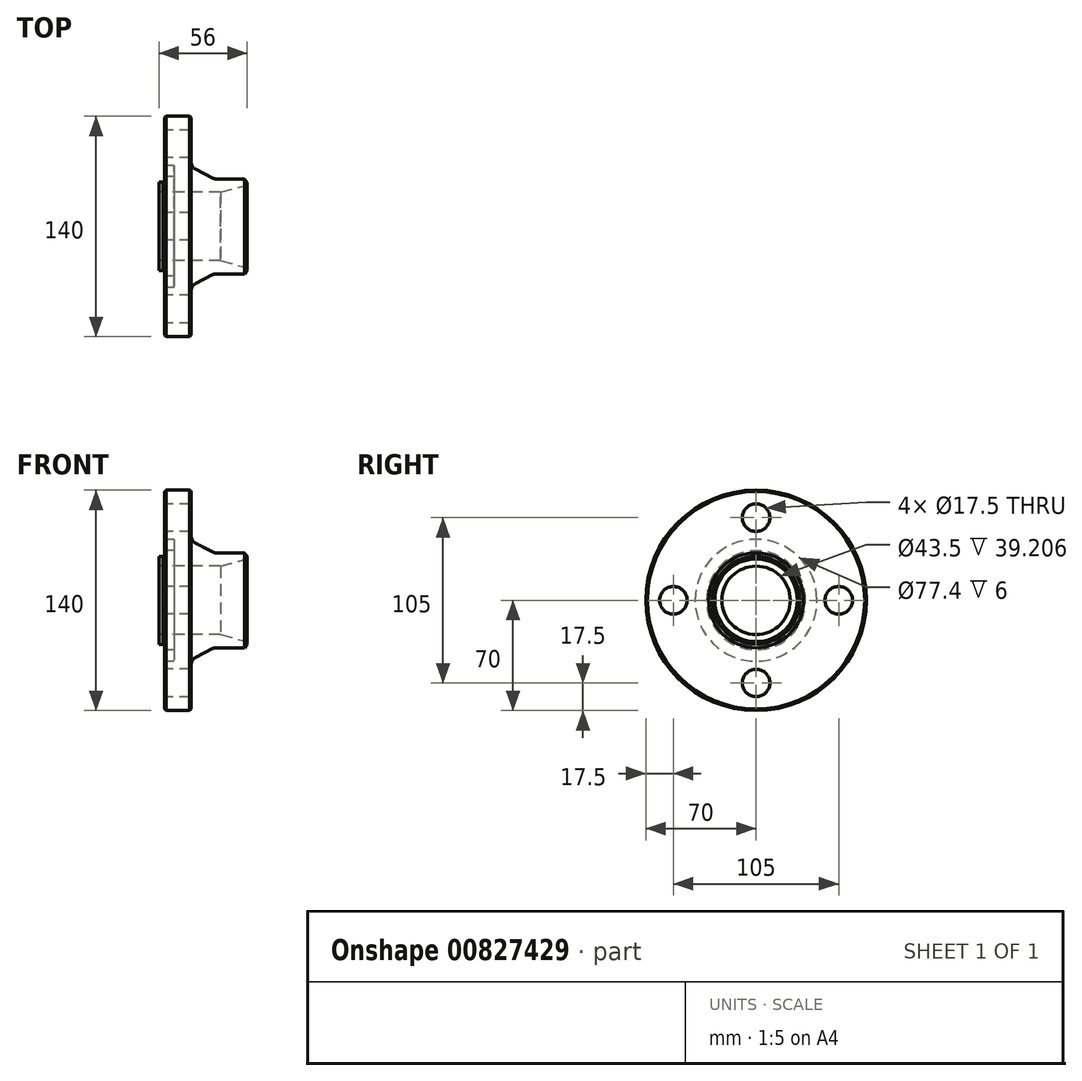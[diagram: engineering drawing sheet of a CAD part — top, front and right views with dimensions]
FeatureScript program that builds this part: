
annotation { "Feature Type Name" : "Feature", "Feature Type Description" : "" }
export const myFeature = defineFeature(function(context is Context, id is Id, definition is map)
    precondition{}
    {
        {
            var Q0;
            Q0=qCreatedBy(makeId("Front.planeOp"),FACE);
            var sketch = newSketch(context, id + "F0", { "sketchPlane" : qUnion([Q0])});
            skLineSegment(sketch, "E0", {"start": v(0, 0) * mm, "end": v(88.97, 0) * mm, "construction": true});
            skLineSegment(sketch, "E1", {"start": v(35.7, 21.75) * mm, "end": v(-3.5, 21.75) * mm});
            skLineSegment(sketch, "E2.trimOffspring", {"start": v(0, 28) * mm, "end": v(0, 31.5) * mm});
            skLineSegment(sketch, "E3", {"start": v(50.73, 30.15) * mm, "end": v(31.58, 30.15) * mm});
            skLineSegment(sketch, "E4", {"start": v(31.58, 30.15) * mm, "end": v(17, 37.7) * mm});
            skLineSegment(sketch, "E5", {"start": v(17, 37.7) * mm, "end": v(17, 70) * mm});
            skLineSegment(sketch, "E6", {"start": v(17, 70) * mm, "end": v(0, 70) * mm});
            skLineSegment(sketch, "E7", {"start": v(0, 31.5) * mm, "end": v(6, 31.5) * mm});
            skLineSegment(sketch, "E8", {"start": v(6, 31.5) * mm, "end": v(6, 38.7) * mm});
            skLineSegment(sketch, "E9", {"start": v(6, 38.7) * mm, "end": v(0, 38.7) * mm});
            skLineSegment(sketch, "E10.trimOffspring", {"start": v(0, 38.7) * mm, "end": v(0, 70) * mm});
            skLineSegment(sketch, "E11", {"start": v(-3.5, 28) * mm, "end": v(-3.5, 21.75) * mm});
            skPoint(sketch, "E12.orphan", {"position": v(0, 21.75) * mm});
            skLineSegment(sketch, "E13", {"start": v(0, 28) * mm, "end": v(-3.5, 28) * mm});
            skLineSegment(sketch, "E14", {"start": v(35.7, 21.75) * mm, "end": v(52.5, 26.25) * mm});
            skLineSegment(sketch, "E15", {"start": v(52.5, 26.25) * mm, "end": v(52.5, 27.84) * mm});
            skLineSegment(sketch, "E16", {"start": v(52.5, 27.84) * mm, "end": v(50.73, 30.15) * mm});
            skSolve(sketch);
        }
        {
            var Q0;
            Q0=makeQuery(id+"F0.imprint","IMPRINT",FACE,{"disambiguationData":[TD([[makeQuery(id+"F0.imprint","IMPRINT",EDGE,{"derivedFrom":sQuery(id+"F0.wireOp",EDGE,"E1")}),-1.0]])]});
            var Q1;
            Q1=sQuery(id+"F0.wireOp",EDGE,"E0");
            revolve(context, id + "F1", {"surfaceOperationType" : NewSurfaceOperationType.NEW, "entities" : qUnion([Q0]), "axis" : qUnion([Q1]), "revolveType" : RevolveType.FULL});
        }
        {
            var Q0;
            Q0=makeQuery(id+"F1.opRevolve","SWEPT_EDGE",EDGE,{"disambiguationData":[OSD([sQuery(id+"F0.wireOp",EDGE,"ZkZXfTss-pbWi-7Jdx-PPOn-aKjTsRns9WXB"),sQuery(id+"F0.wireOp",EDGE,"QTMTy84d-BkUg-pJvk-3l4K-4WQvV4doNcmV")])]});
            var Q1;
            Q1=makeQuery(id+"F1.opRevolve","SWEPT_EDGE",EDGE,{"disambiguationData":[OSD([sQuery(id+"F0.wireOp",EDGE,"ZkZXfTss-pbWi-7Jdx-PPOn-aKjTsRns9WXB"),sQuery(id+"F0.wireOp",EDGE,"E2.trimOffspring")])]});
            chamfer(context, id + "F2", {"entities" : qUnion([Q0, Q1]), "width" : 1 * mm, "tangentPropagation" : true});
        }
        {
            var Q0;
            Q0=makeQuery(id+"F1.opRevolve","SWEPT_EDGE",EDGE,{"disambiguationData":[OSD([sQuery(id+"F0.wireOp",EDGE,"E5"),sQuery(id+"F0.wireOp",EDGE,"E6")])]});
            var Q1;
            Q1=makeQuery(id+"F1.opRevolve","SWEPT_EDGE",EDGE,{"disambiguationData":[OSD([sQuery(id+"F0.wireOp",EDGE,"E6"),sQuery(id+"F0.wireOp",EDGE,"E10.trimOffspring")])]});
            chamfer(context, id + "F3", {"entities" : qUnion([Q0, Q1]), "width" : 1 * mm, "tangentPropagation" : true});
        }
        {
            var Q0;
            Q0=makeQuery(id+"F1.opRevolve","SWEPT_EDGE",EDGE,{"disambiguationData":[OSD([sQuery(id+"F0.wireOp",EDGE,"E4"),sQuery(id+"F0.wireOp",EDGE,"E5")])]});
            var Q1;
            Q1=makeQuery(id+"F1.opRevolve","SWEPT_EDGE",EDGE,{"disambiguationData":[OSD([sQuery(id+"F0.wireOp",EDGE,"E3"),sQuery(id+"F0.wireOp",EDGE,"E4")])]});
            fillet(context, id + "F4", {"entities" : qUnion([Q0, Q1]), "radius" : 5 * mm, "tangentPropagation" : true, "allowEdgeOverflow" : false});
        }
        {
            var Q0;
            Q0=makeQuery(id+"F1.opRevolve","SWEPT_FACE",FACE,{"disambiguationData":[OSD([sQuery(id+"F0.wireOp",EDGE,"E10.trimOffspring")])]});
            var sketch = newSketch(context, id + "F5", { "sketchPlane" : qUnion([Q0])});
            skCircle(sketch, "E17", {"center": v(0, 0) * mm, "radius": 52.5 * mm, "construction": true});
            skCircle(sketch, "E18", {"center": v(0, 52.5) * mm, "radius": 8.75 * mm});
            skCircle(sketch, "E19.1.0", {"center": v(-52.5, 0) * mm, "radius": 8.75 * mm});
            skCircle(sketch, "E19.2.0", {"center": v(0, -52.5) * mm, "radius": 8.75 * mm});
            skCircle(sketch, "E19.3.0", {"center": v(52.5, 0) * mm, "radius": 8.75 * mm});
            skSolve(sketch);
        }
        {
            var Q0;
            Q0=makeQuery(id+"F5.imprint","IMPRINT",FACE,{"disambiguationData":[TD([[makeQuery(id+"F5.imprint","IMPRINT",EDGE,{"derivedFrom":sQuery(id+"F5.wireOp",EDGE,"E18")}),1.0]])]});
            var Q1;
            Q1=makeQuery(id+"F5.imprint","IMPRINT",FACE,{"disambiguationData":[TD([[makeQuery(id+"F5.imprint","IMPRINT",EDGE,{"derivedFrom":sQuery(id+"F5.wireOp",EDGE,"E19.1.0")}),1.0]])]});
            var Q2;
            Q2=makeQuery(id+"F5.imprint","IMPRINT",FACE,{"disambiguationData":[TD([[makeQuery(id+"F5.imprint","IMPRINT",EDGE,{"derivedFrom":sQuery(id+"F5.wireOp",EDGE,"E19.3.0")}),1.0]])]});
            var Q3;
            Q3=makeQuery(id+"F5.imprint","IMPRINT",FACE,{"disambiguationData":[TD([[makeQuery(id+"F5.imprint","IMPRINT",EDGE,{"derivedFrom":sQuery(id+"F5.wireOp",EDGE,"E19.2.0")}),1.0]])]});
            extrude(context, id + "F6", {"entities" : qUnion([Q0, Q1, Q2, Q3]), "operationType" : NewBodyOperationType.REMOVE, "endBound" : BoundingType.THROUGH_ALL, "oppositeDirection" : true, "depth" : 25 * mm, "offsetDistance" : 25 * mm});
        }
    });
